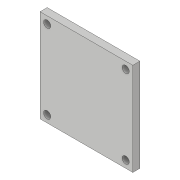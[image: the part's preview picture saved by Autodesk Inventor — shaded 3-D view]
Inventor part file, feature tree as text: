
AUTODESK INVENTOR PART (.ipt)
format: ipt  version: 2019 (Build 230136000, 136)  size: 112,640 bytes
history: native  units: in
note: dims shown in document units (in); Inventor stores cm internally (conversion verified against a paired STEP export)
features: extrude x3, sketch x2
ambient origin geometry x8: Origin, YZ Plane, XZ Plane, XY Plane, X Axis, Y Axis, Z Axis, Center Point
bodies: Solid1 (feature_tree)
feature tree (5):
  extrude  "Extrusion1"  Depth=5.1181in
  extrude  "Extrusion2"  Depth=0.3937in
  extrude  "Extrusion3"  Depth=0.3937in
  sketch  "Sketch1"  dims[d0=5.1181in d1=5.1181in]
  sketch  "Sketch2"  dims[d2=0.3937in d3=0.0in d4=0.3937in d5=4.7244in d6=4.3307in d7=4.3307in d8=4.3307in d9=0.3937in d10=0.3937in d11=0.3937in d12=0.3937in d13=0.3937in d14=0.0in d15=2.5591in d16=1.1811in d17=0.4331in d18=2.5591in d19=1.378in d21=0.3937in d22=0.0in d23=1.9685in d24=2.3622in]
